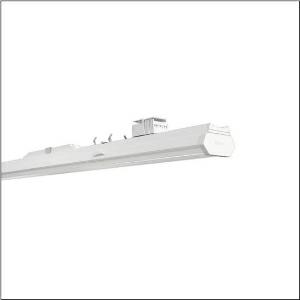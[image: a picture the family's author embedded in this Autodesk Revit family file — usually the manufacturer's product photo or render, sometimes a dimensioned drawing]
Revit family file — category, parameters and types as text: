
# Revit family: licross_r__21_protected_ho_52tp12mn4e5m_b3cb
name_source: partatom
category: Lighting Fixtures
units: mm (PartAtom-declared; Revit-internal decimal feet)

## family parameters
Cut with Voids When Loaded = No
Host = Face
Light Source = No
Part Type = Normal
Room Calculation Point = No
Round Connector Dimension = Use Diameter
Shared = No

## types (1)
- --- (1 x LED, 14780 lm, 83.2 W, 4000K)
    Apparent Load = 83 VA
    CIE Flux Codes = 70 91 97 98 100
    Color Rendering = 80
    Color Temperature = 4000K
    Default Elevation = 1800 mm
    Description = Licross® 21 Protected HO, luminaire insert, of sheet steel, galvanised, coil coated, white, length: 1.500mm, width: 90mm, height: 101mm, LED rated luminous flux: 14.790lm, light colour: 840, control gear: ON/OFF Multilumen, with plug, 3-pole, with phase selection, mains connection: 220..240V, AC, 50/60Hz, rated input power: 83W, halogen-free wiring, primary light control with lens, of plastic, primary optical cover: cover, of PMMA, light emission: direct distribution, primary light characteristic: symmetric, protection rating (complete): IP64, insulation class (complete): insulation class I (protective earthing), certification: CE, ENEC, VDE, UKCA, protection symbol: D if used in an environment with conductive dust loads with corresponding accessories, impact resistance: IK06, permissible ambient temperature for indoor applications: -35..+35°C, corresponds to IFS (International Featured Standards) requirements for safety and quality in the food industry, reducing of maximum allowable ambient temperature of 5°C with ceiling mounting, LABS conformity tested according to VDMA 24364:2018-05, packaging unit: 1 piece
    Height = 92 mm
    Lamp = 1 x LED
    Lamp Light Flux = 14780 lm
    Lamp Power = 83.2 W
    Lamp count = 1
    Length = 1500 mm
    Luminous efficacy = 178 lm/W
    Manufacturer = Siteco
    ModVariant = No
    Model = 52TP12MN4E5M
    Mounting Place = Ceiling
    Mounting Type = Pendant
    Number of Poles = 1
    OnlyDefault = Yes
    Power Factor = 1
    Product Name = Licross® 21 Protected HO
    Product group = luminaire insert
    ProductGroupID = 902
    Protection Class = Protection class I
    Protection Degree = IP 64
    RLX_Detail_Level = 1
    RLX_Emergency_Light_Flux = 0 lm
    RLX_Emergency_Type = 0
    RLX_Emergency_Type_DB = No
    RlxData = <blob elided: 21985 chars, md5=a3636cbc>
    Socket = socket
    Standby Power = 0 W
    System Light Flux = 14780 lm
    System Power = 83 W
    Type Comments = factory setting: luminous flux: 100 % | (A | C | E) | 195 mA
    Type Image = l_1256148.jpg
    URL = http://relux.com
    VarID = @adj_109158
    Voltage = 0 V
    Weight = 0.00 kg
    Width = 88 mm

## geometry (parser evidence)
native form markers: Blend x4, Sweep x10
no freeform markers — native parametric forms only
